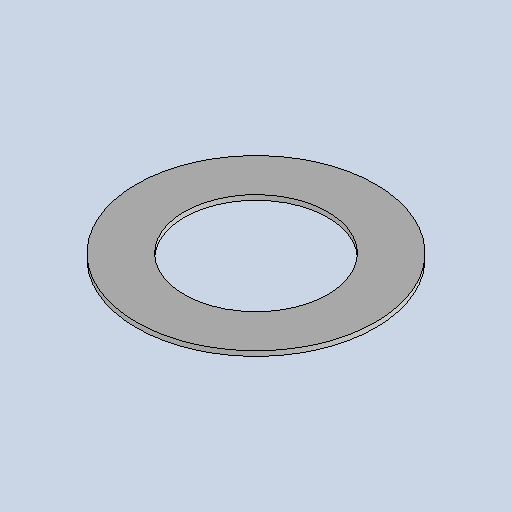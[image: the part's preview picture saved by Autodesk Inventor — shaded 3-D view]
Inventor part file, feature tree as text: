
AUTODESK INVENTOR PART (.ipt)
format: ipt  version: 2025 (Build 290162010, 162A)  size: 94,720 bytes
history: native  units: mm
features: other x2, sheet_metal_op x1, sketch x1
ambient origin geometry x8: Origin, YZ Plane, XZ Plane, XY Plane, X Axis, Y Axis, Z Axis, Center Point
bodies: Solid1 (feature_tree)
feature tree (4):
  other  "MSC 0392 flange"
  sheet_metal_op  "Face1"
  sketch  "Sketch1"  dims[d0=89.9mm d1=149.9mm d2=3.048mm]
  other  "Plate1"
